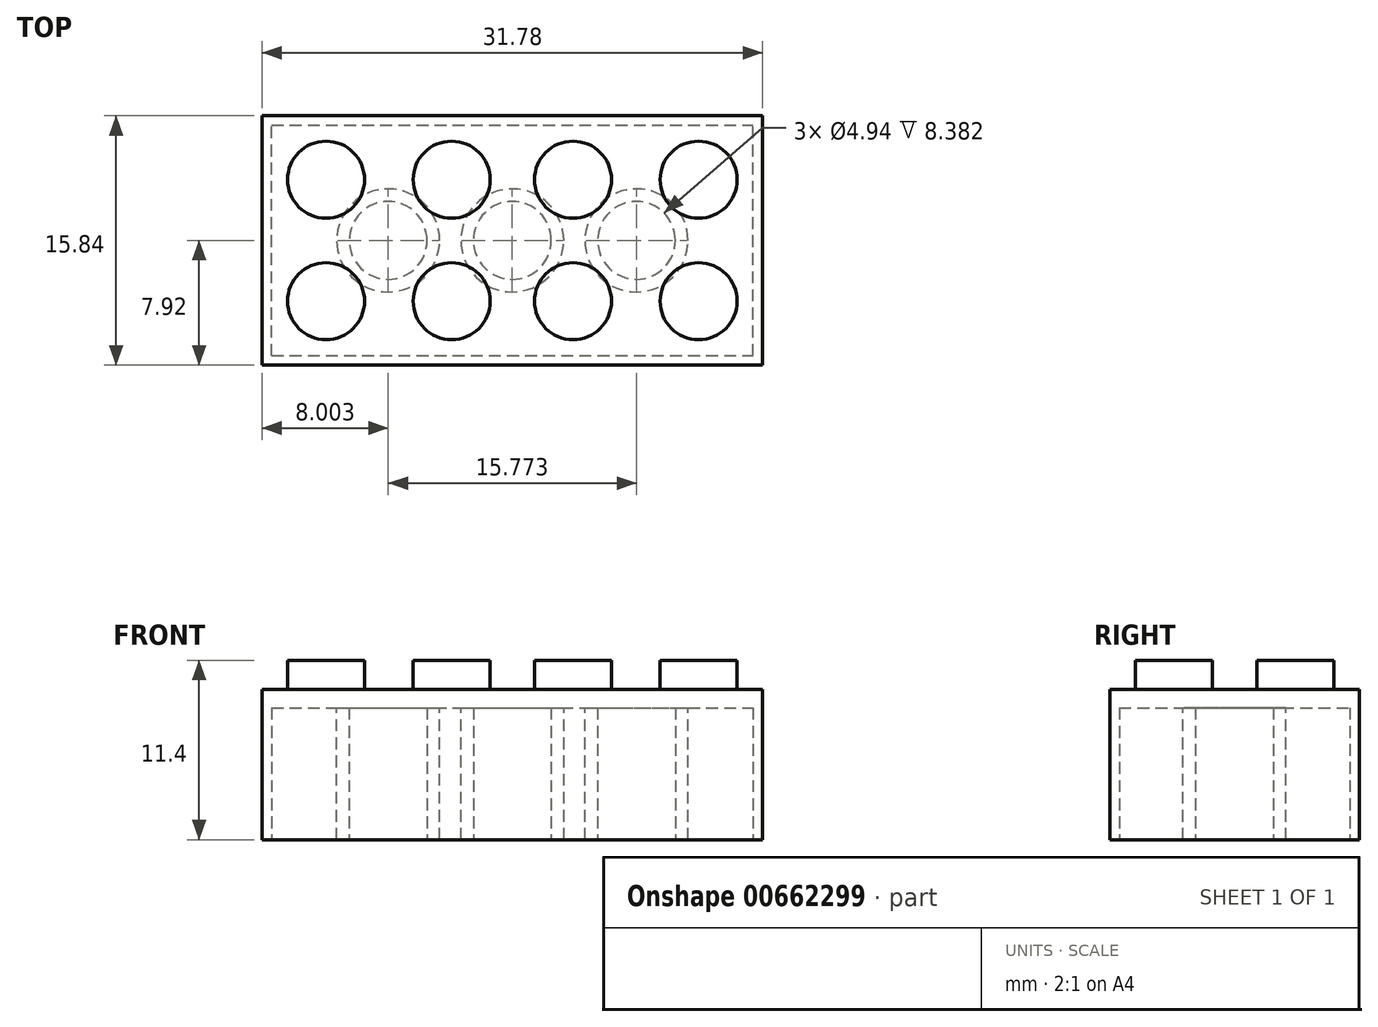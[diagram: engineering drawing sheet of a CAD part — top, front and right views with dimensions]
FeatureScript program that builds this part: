
annotation { "Feature Type Name" : "Feature", "Feature Type Description" : "" }
export const myFeature = defineFeature(function(context is Context, id is Id, definition is map)
    precondition{}
    {
        {
            var Q0;
            Q0=qCreatedBy(makeId("Top.planeOp"),FACE);
            var sketch = newSketch(context, id + "F0", { "sketchPlane" : qUnion([Q0])});
            skLineSegment(sketch, "E0.bottom", {"start": v(-15.89, 7.92) * mm, "end": v(15.89, 7.92) * mm});
            skLineSegment(sketch, "E0.top", {"start": v(-15.89, -7.92) * mm, "end": v(15.89, -7.92) * mm});
            skLineSegment(sketch, "E0.left", {"start": v(-15.89, 7.92) * mm, "end": v(-15.89, -7.92) * mm});
            skLineSegment(sketch, "E0.right", {"start": v(15.89, 7.92) * mm, "end": v(15.89, -7.92) * mm});
            skPoint(sketch, "E0.middle", {"position": v(0, 0) * mm});
            skSolve(sketch);
        }
        {
            var Q0;
            Q0=qSketchRegion(id+"F0",true);
            extrude(context, id + "F1", {"entities" : qUnion([Q0]), "depth" : 9.54 * mm, "offsetDistance" : 25.4 * mm});
        }
        {
            var Q0;
            Q0=makeQuery(id+"F1.opExtrude","CAP_FACE",FACE,{"disambiguationData":[OSD([sQuery(id+"F0.wireOp",EDGE,"E0.bottom"),sQuery(id+"F0.wireOp",EDGE,"E0.top"),sQuery(id+"F0.wireOp",EDGE,"E0.left"),sQuery(id+"F0.wireOp",EDGE,"E0.right")])],"isStart":false});
            var sketch = newSketch(context, id + "F2", { "sketchPlane" : qUnion([Q0])});
            skCircle(sketch, "E1", {"center": v(-11.83, 3.86) * mm, "radius": 2.44 * mm});
            skCircle(sketch, "E2", {"center": v(-3.85, 3.86) * mm, "radius": 2.44 * mm});
            skCircle(sketch, "E3", {"center": v(3.85, 3.86) * mm, "radius": 2.44 * mm});
            skCircle(sketch, "E4", {"center": v(11.83, 3.86) * mm, "radius": 2.44 * mm});
            skCircle(sketch, "E5", {"center": v(11.83, -3.86) * mm, "radius": 2.44 * mm});
            skCircle(sketch, "E6", {"center": v(3.85, -3.86) * mm, "radius": 2.44 * mm});
            skCircle(sketch, "E7", {"center": v(-3.85, -3.86) * mm, "radius": 2.44 * mm});
            skCircle(sketch, "E8", {"center": v(-11.83, -3.86) * mm, "radius": 2.44 * mm});
            skSolve(sketch);
        }
        {
            var Q0;
            Q0=makeQuery(id+"F2.imprint","IMPRINT",FACE,{"disambiguationData":[TD([[makeQuery(id+"F2.imprint","IMPRINT",EDGE,{"derivedFrom":sQuery(id+"F2.wireOp",EDGE,"E1")}),1.0]])]});
            var Q1;
            Q1=makeQuery(id+"F2.imprint","IMPRINT",FACE,{"disambiguationData":[TD([[makeQuery(id+"F2.imprint","IMPRINT",EDGE,{"derivedFrom":sQuery(id+"F2.wireOp",EDGE,"E2")}),1.0]])]});
            var Q2;
            Q2=makeQuery(id+"F2.imprint","IMPRINT",FACE,{"disambiguationData":[TD([[makeQuery(id+"F2.imprint","IMPRINT",EDGE,{"derivedFrom":sQuery(id+"F2.wireOp",EDGE,"E3")}),1.0]])]});
            var Q3;
            Q3=makeQuery(id+"F2.imprint","IMPRINT",FACE,{"disambiguationData":[TD([[makeQuery(id+"F2.imprint","IMPRINT",EDGE,{"derivedFrom":sQuery(id+"F2.wireOp",EDGE,"E4")}),1.0]])]});
            var Q4;
            Q4=makeQuery(id+"F2.imprint","IMPRINT",FACE,{"disambiguationData":[TD([[makeQuery(id+"F2.imprint","IMPRINT",EDGE,{"derivedFrom":sQuery(id+"F2.wireOp",EDGE,"E8")}),1.0]])]});
            var Q5;
            Q5=makeQuery(id+"F2.imprint","IMPRINT",FACE,{"disambiguationData":[TD([[makeQuery(id+"F2.imprint","IMPRINT",EDGE,{"derivedFrom":sQuery(id+"F2.wireOp",EDGE,"E7")}),1.0]])]});
            var Q6;
            Q6=makeQuery(id+"F2.imprint","IMPRINT",FACE,{"disambiguationData":[TD([[makeQuery(id+"F2.imprint","IMPRINT",EDGE,{"derivedFrom":sQuery(id+"F2.wireOp",EDGE,"E6")}),1.0]])]});
            var Q7;
            Q7=makeQuery(id+"F2.imprint","IMPRINT",FACE,{"disambiguationData":[TD([[makeQuery(id+"F2.imprint","IMPRINT",EDGE,{"derivedFrom":sQuery(id+"F2.wireOp",EDGE,"E5")}),1.0]])]});
            extrude(context, id + "F3", {"entities" : qUnion([Q0, Q1, Q2, Q3, Q4, Q5, Q6, Q7]), "operationType" : NewBodyOperationType.ADD, "depth" : 1.87 * mm, "offsetDistance" : 25.4 * mm});
        }
        {
            var Q0;
            Q0=makeQuery(id+"F1.opExtrude","CAP_FACE",FACE,{"disambiguationData":[OSD([sQuery(id+"F0.wireOp",EDGE,"E0.bottom"),sQuery(id+"F0.wireOp",EDGE,"E0.top"),sQuery(id+"F0.wireOp",EDGE,"E0.left"),sQuery(id+"F0.wireOp",EDGE,"E0.right")])],"isStart":true});
            var Q1;
            Q1=qCreatedBy(makeId("Origin.pointOp"),VERTEX);
            cPlane(context, id + "F4", {"entities" : qUnion([Q0, Q1]), "cplaneType" : CPlaneType.PLANE_POINT, "offset" : 25.4 * mm, "width" : 152.4 * mm, "height" : 152.4 * mm});
        }
        {
            var Q0;
            Q0=qCreatedBy(id+"F4.planeOp",FACE);
            var sketch = newSketch(context, id + "F5", { "sketchPlane" : qUnion([Q0])});
            skLineSegment(sketch, "E9.bottom", {"start": v(-15.28, 7.32) * mm, "end": v(15.28, 7.32) * mm});
            skLineSegment(sketch, "E9.top", {"start": v(-15.28, -7.32) * mm, "end": v(15.28, -7.32) * mm});
            skLineSegment(sketch, "E9.left", {"start": v(-15.28, 7.32) * mm, "end": v(-15.28, -7.32) * mm});
            skLineSegment(sketch, "E9.right", {"start": v(15.28, 7.32) * mm, "end": v(15.28, -7.32) * mm});
            skPoint(sketch, "E9.middle", {"position": v(0, 0) * mm});
            skSolve(sketch);
        }
        {
            var Q0;
            Q0=qSketchRegion(id+"F5",true);
            extrude(context, id + "F6", {"entities" : qUnion([Q0]), "operationType" : NewBodyOperationType.REMOVE, "oppositeDirection" : true, "depth" : 8.38 * mm, "offsetDistance" : 25.4 * mm});
        }
        {
            var Q0;
            Q0=makeQuery(id+"F6.boolean.opBoolean","COPY",FACE,{"derivedFrom":makeQuery(id+"F6.opExtrude","CAP_FACE",FACE,{"disambiguationData":[OSD([sQuery(id+"F5.wireOp",EDGE,"E9.bottom"),sQuery(id+"F5.wireOp",EDGE,"E9.top"),sQuery(id+"F5.wireOp",EDGE,"E9.left"),sQuery(id+"F5.wireOp",EDGE,"E9.right")])],"isStart":false})});
            var sketch = newSketch(context, id + "F7", { "sketchPlane" : qUnion([Q0])});
            skCircle(sketch, "E10", {"center": v(0, 0) * mm, "radius": 3.27 * mm});
            skCircle(sketch, "E11", {"center": v(-7.89, 0) * mm, "radius": 3.27 * mm});
            skCircle(sketch, "E12", {"center": v(7.89, 0) * mm, "radius": 3.27 * mm});
            skSolve(sketch);
        }
        {
            var Q0;
            Q0=makeQuery(id+"F7.imprint","IMPRINT",FACE,{"disambiguationData":[TD([[makeQuery(id+"F7.imprint","IMPRINT",EDGE,{"derivedFrom":sQuery(id+"F7.wireOp",EDGE,"E11")}),1.0]])]});
            var Q1;
            Q1=makeQuery(id+"F7.imprint","IMPRINT",FACE,{"disambiguationData":[TD([[makeQuery(id+"F7.imprint","IMPRINT",EDGE,{"derivedFrom":sQuery(id+"F7.wireOp",EDGE,"E10")}),1.0]])]});
            var Q2;
            Q2=makeQuery(id+"F7.imprint","IMPRINT",FACE,{"disambiguationData":[TD([[makeQuery(id+"F7.imprint","IMPRINT",EDGE,{"derivedFrom":sQuery(id+"F7.wireOp",EDGE,"E12")}),1.0]])]});
            extrude(context, id + "F8", {"entities" : qUnion([Q0, Q1, Q2]), "operationType" : NewBodyOperationType.ADD, "depth" : 8.38 * mm, "offsetDistance" : 25.4 * mm});
        }
        {
            var Q0;
            Q0=makeQuery(id+"F8.opExtrude","CAP_FACE",FACE,{"disambiguationData":[OSD([sQuery(id+"F7.wireOp",EDGE,"E10")])],"isStart":false});
            var sketch = newSketch(context, id + "F9", { "sketchPlane" : qUnion([Q0])});
            skCircle(sketch, "E13", {"center": v(-7.89, 0) * mm, "radius": 2.47 * mm});
            skCircle(sketch, "E14", {"center": v(0, 0) * mm, "radius": 2.47 * mm});
            skCircle(sketch, "E15", {"center": v(7.89, 0) * mm, "radius": 2.47 * mm});
            skSolve(sketch);
        }
        {
            var Q0;
            Q0=makeQuery(id+"F9.imprint","IMPRINT",FACE,{"disambiguationData":[TD([[makeQuery(id+"F9.imprint","IMPRINT",EDGE,{"derivedFrom":sQuery(id+"F9.wireOp",EDGE,"E13")}),1.0]])]});
            var Q1;
            Q1=makeQuery(id+"F9.imprint","IMPRINT",FACE,{"disambiguationData":[TD([[makeQuery(id+"F9.imprint","IMPRINT",EDGE,{"derivedFrom":sQuery(id+"F9.wireOp",EDGE,"E14")}),1.0]])]});
            var Q2;
            Q2=makeQuery(id+"F9.imprint","IMPRINT",FACE,{"disambiguationData":[TD([[makeQuery(id+"F9.imprint","IMPRINT",EDGE,{"derivedFrom":sQuery(id+"F9.wireOp",EDGE,"E15")}),1.0]])]});
            extrude(context, id + "F10", {"entities" : qUnion([Q0, Q1, Q2]), "operationType" : NewBodyOperationType.REMOVE, "oppositeDirection" : true, "depth" : 8.38 * mm, "offsetDistance" : 25.4 * mm});
        }
    });
